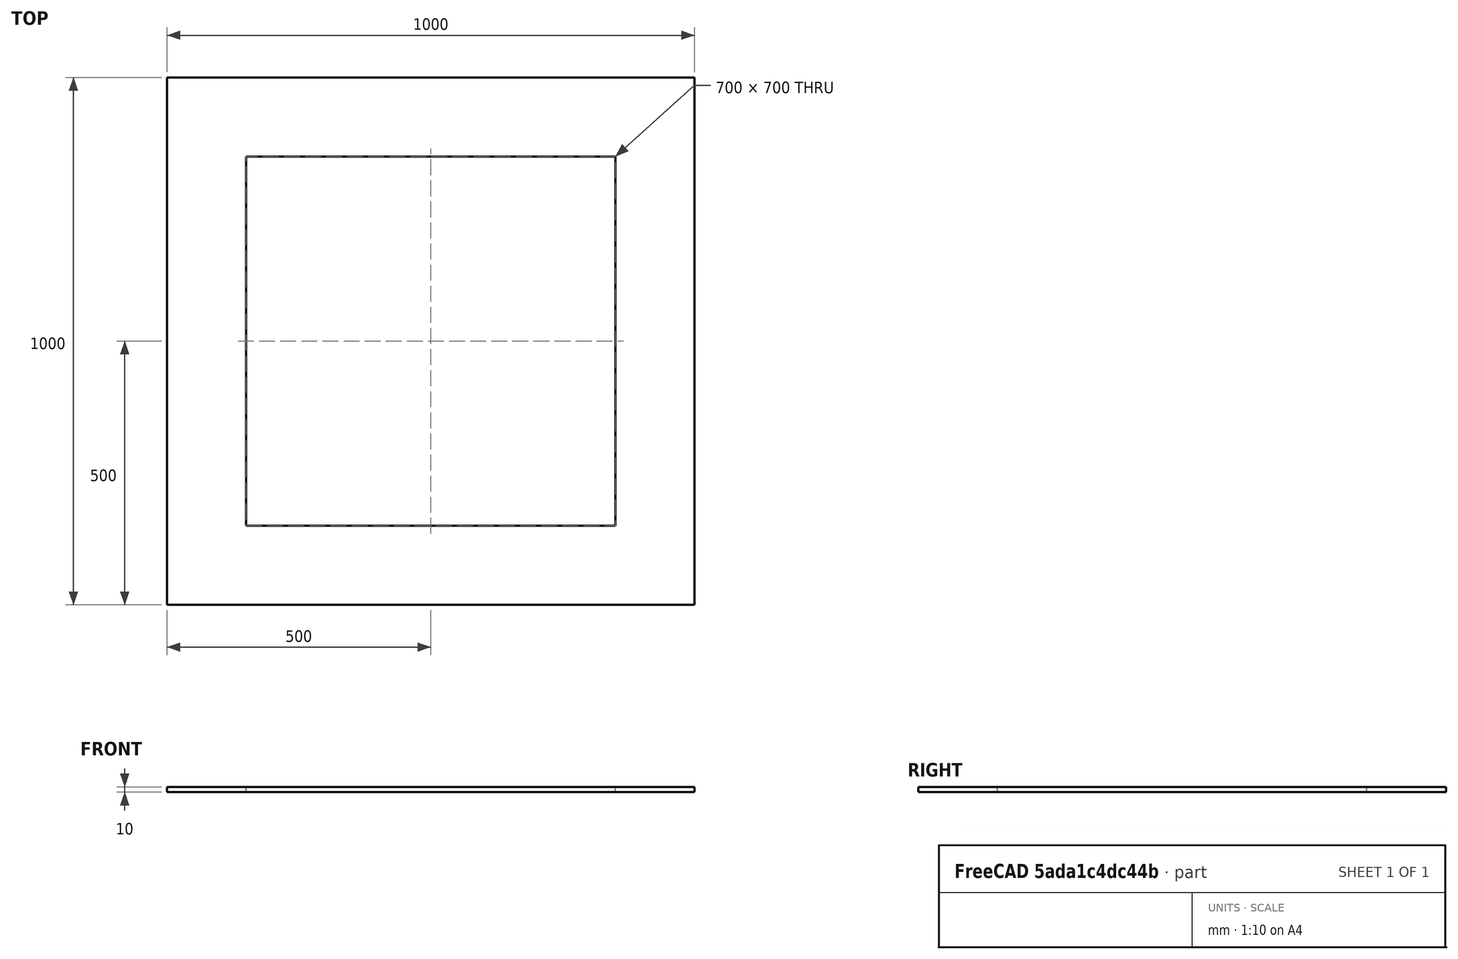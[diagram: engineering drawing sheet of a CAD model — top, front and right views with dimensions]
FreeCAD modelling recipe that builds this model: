
FCSTD DOCUMENT  (FreeCAD 0.21R33694 (Git))
Label: shear_panel_with_square_hole
License: All rights reserved
LicenseURL: http://en.wikipedia.org/wiki/All_rights_reserved
objects: Fem::ConstraintForce×6, Part::Box×2, Fem::ConstraintDisplacement×2, App::MaterialObjectPython×1, Fem::FemSolverObjectPython×1, Fem::ConstraintFixed×1, Part::Cut×1, Fem::FemMeshObjectPython×1, Fem::FemAnalysis×1
note: 3 computed .brp shape members not serialized (recipe doc carries the construction recipe); baked Part::Feature solids carry a one-line shape summary decoded from their .brp

FEATURE [Part::Box] Box  label="Cube"
  AttacherType = Attacher::AttachEngine3D
  Height = 10
  Length = 1000
  Width = 1000
FEATURE [Fem::ConstraintDisplacement] ConstraintDisplacement
  NormalDirection = (0,0,1)
  Normals = (16) [(0,0,1),(0,0,1),(0,0,1),(0,0,1),(0,0,1),(0,0,1),(0,0,1),(0,0,1),(0,0,1),(0,0,1),(0,0,1),(0,0,1),(0,0,1),(0,0,1),(0,0,1),(0,0,1)]
  Points = (16) [(0,0,0),(333.333,0,0),(666.667,0,0),(1000,0,0),(0,0,0),(0,333.333,0),(0,666.667,0),(0,1000,0),(1000,0,0),(1000,333.333,0),(1000,666.667,0),+5 more]
  References = -> [Box]
  Scale = 33
  hasXFormula = false
  hasYFormula = false
  hasZFormula = false
  rotxFix = false
  rotxFree = true
  rotyFix = false
  rotyFree = true
  rotzFix = false
  rotzFree = true
  useFlowSurfaceForce = false
  xDisplacement = 0
  xFix = false
  xFree = true
  xRotation = 0
  yDisplacement = 0
  yFix = false
  yFree = true
  yRotation = 0
  zDisplacement = 0
  zFix = false
  zFree = false
  zRotation = 0
FEATURE [Fem::ConstraintForce] ConstraintForce
  Direction = -> Box [Edge12]
  DirectionVector = (1,0,0)
  Force = 1000000
  NormalDirection = (0,1,0)
  Points = (15) [(0,1000,0),(0,1000,5),(0,1000,10),(250,1000,0),(250,1000,5),(250,1000,10),(500,1000,0),(500,1000,5),(500,1000,10),(750,1000,0),(750,1000,5),+4 more]
  References = -> [Box]
FEATURE [Fem::ConstraintForce] ConstraintForce001
  Direction = -> Box [Edge10]
  DirectionVector = (-1,0,0)
  Force = 1000000
  NormalDirection = (0,-1,0)
  Points = (15) [(0,0,0),(0,0,5),(0,0,10),(250,0,0),(250,0,5),(250,0,10),(500,0,0),(500,0,5),(500,0,10),(750,0,0),(750,0,5),(750,0,10),(1000,0,0),(1000,0,5),+1 more]
  References = -> [Box]
  Reversed = true
FEATURE [Fem::ConstraintForce] ConstraintForce002
  Direction = -> Box [Edge6]
  DirectionVector = (0,1,0)
  Force = 1000000
  NormalDirection = (1,0,0)
  Points = (15) [(1000,1000,0),(1000,1000,5),(1000,1000,10),(1000,750,0),(1000,750,5),(1000,750,10),(1000,500,0),(1000,500,5),(1000,500,10),(1000,250,0),(1000,250,5),+4 more]
  References = -> [Box]
FEATURE [Fem::ConstraintForce] ConstraintForce003
  Direction = -> Box [Edge2]
  DirectionVector = (0,-1,0)
  Force = 1000000
  NormalDirection = (-1,0,0)
  Points = (15) [(0,1000,0),(0,1000,5),(0,1000,10),(0,750,0),(0,750,5),(0,750,10),(0,500,0),(0,500,5),(0,500,10),(0,250,0),(0,250,5),(0,250,10),(0,0,0),(0,0,5),+1 more]
  References = -> [Box]
  Reversed = true
FEATURE [App::MaterialObjectPython] MaterialSolid  # material (typed FeaturePython)
  Category = 0
  Material = AuthorAndLicense=(c) 2014 M. Münch - GNU Lesser General Public License (LGPL),CardName=Steel-St-E-315,Density=7800 kg/m^3,Father=Metal,+13 more (map truncated)
FEATURE [Fem::FemSolverObjectPython] SolverCcxTools  # FEM object (typed FeaturePython)
  AnalysisType = 0
  BeamShellResultOutput3D = false
  BucklingFactors = 1
  EigenmodeHighLimit = 1000000
  EigenmodeLowLimit = 0
  EigenmodesCount = 10
  GeometricalNonlinearity = 0
  IterationsControlParameterCutb = 0.25,0.5,0.75,0.85,,,1.5,
  IterationsControlParameterIter = 4,8,9,200,10,400,,200,,
  IterationsControlParameterTimeUse = false
  IterationsThermoMechMaximum = 2000
  IterationsUserDefinedIncrementations = false
  IterationsUserDefinedTimeStepLength = false
  MaterialNonlinearity = 0
  MatrixSolverType = 0
  SplitInputWriter = false
  ThermoMechSteadyState = true
  TimeEnd = 1
  TimeInitialStep = 0.01
FEATURE [Fem::ConstraintFixed] ConstraintFixed
  NormalDirection = (0,0,1)
  Normals = (2) [(0,0,1),(0,0,1)]
  Points = (2) [(1000,1000,0),(1000,1000,10)]
  References = -> [Box]
FEATURE [Fem::ConstraintDisplacement] ConstraintDisplacement001
  NormalDirection = (0,0,1)
  Normals = (2) [(0,0,1),(0,0,1)]
  Points = (2) [(1000,0,0),(1000,0,10)]
  References = -> [Box]
  hasXFormula = false
  hasYFormula = false
  hasZFormula = false
  rotxFix = false
  rotxFree = true
  rotyFix = false
  rotyFree = true
  rotzFix = false
  rotzFree = true
  useFlowSurfaceForce = false
  xDisplacement = 0
  xFix = false
  xFree = false
  xRotation = 0
  yDisplacement = 0
  yFix = false
  yFree = true
  yRotation = 0
  zDisplacement = 0
  zFix = false
  zFree = true
  zRotation = 0
FEATURE [Fem::ConstraintForce] ConstraintForce004
  DirectionVector = (0,1,0)
  Force = 1
  NormalDirection = (0,-1,0)
  Reversed = true
FEATURE [Fem::ConstraintForce] ConstraintForce005
  DirectionVector = (0,-1,0)
  Force = 1
  NormalDirection = (0,1,0)
  Reversed = true
FEATURE [Part::Box] Box001  label="Cube001"
  AttacherType = Attacher::AttachEngine3D
  Height = 10
  Length = 700
  Placement = pos=(150,150,0) rot=(0,0,1;0rad)
  Width = 700
FEATURE [Part::Cut] Cut
  Base = -> Box
  Tool = -> Box001
FEATURE [Fem::FemMeshObjectPython] FEMMeshGmsh  # FEM object (typed FeaturePython)
  Algorithm2D = 0
  Algorithm3D = 0
  CharacteristicLengthMax = 50
  CharacteristicLengthMin = 0
  CoherenceMesh = true
  ElementDimension = 0
  ElementOrder = 1
  GeometryTolerance = 1e-06
  GroupsOfNodes = false
  HighOrderOptimize = 0
  MeshSizeFromCurvature = 12
  OptimizeNetgen = false
  OptimizeStd = true
  Part = -> Cut
  RecombinationAlgorithm = 0
  Recombine3DAll = false
  RecombineAll = false
  SecondOrderLinear = false
FEATURE [Fem::FemAnalysis] Analysis
  Group = -> [ConstraintDisplacement,ConstraintForce,ConstraintForce001,ConstraintForce002,ConstraintForce003,MaterialSolid,SolverCcxTools,ConstraintFixed,ConstraintDisplacement001,ConstraintForce004,ConstraintForce005,FEMMeshGmsh]
